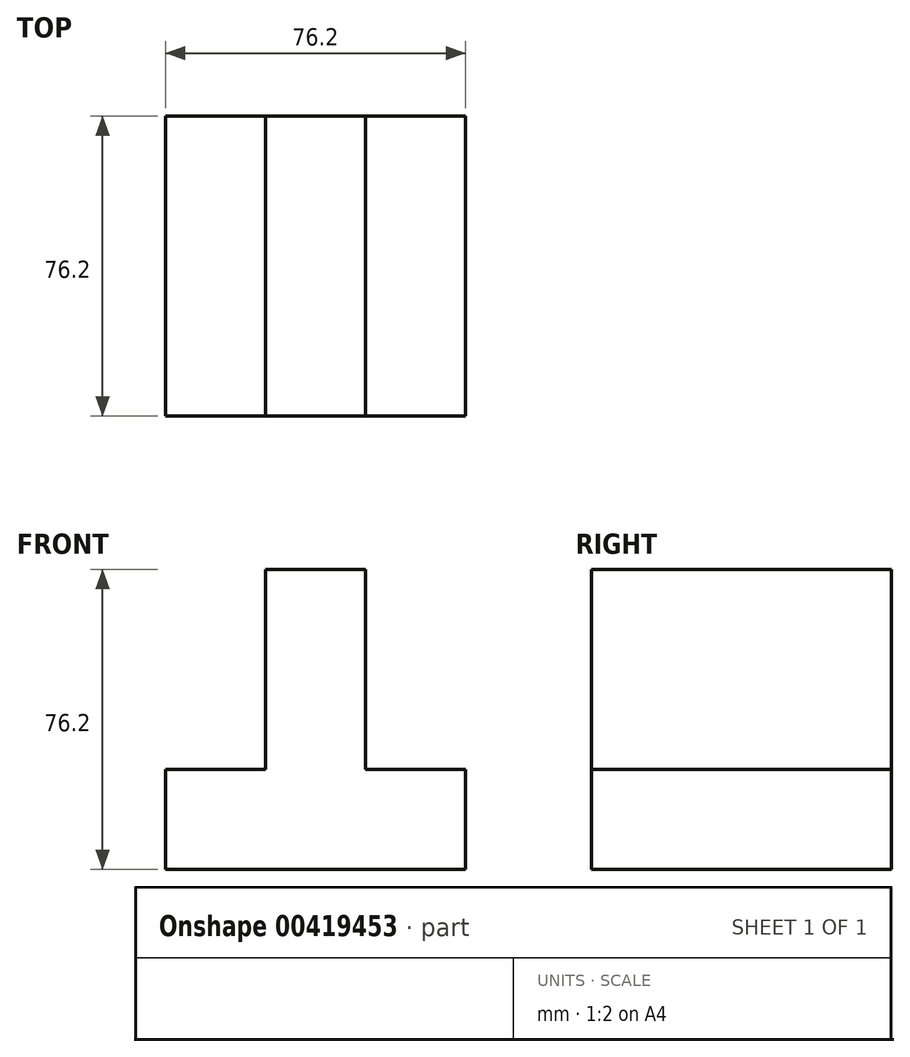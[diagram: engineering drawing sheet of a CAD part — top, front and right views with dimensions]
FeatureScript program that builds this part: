
annotation { "Feature Type Name" : "Feature", "Feature Type Description" : "" }
export const myFeature = defineFeature(function(context is Context, id is Id, definition is map)
    precondition{}
    {
        {
            var Q0;
            Q0=qCreatedBy(makeId("Front.planeOp"),FACE);
            var sketch = newSketch(context, id + "F0", { "sketchPlane" : qUnion([Q0])});
            skLineSegment(sketch, "E0", {"start": v(-36.92, -45.54) * mm, "end": v(39.28, -45.54) * mm});
            skLineSegment(sketch, "E1", {"start": v(39.28, -45.54) * mm, "end": v(39.28, -20.14) * mm});
            skLineSegment(sketch, "E2", {"start": v(39.28, -20.14) * mm, "end": v(13.88, -20.14) * mm});
            skLineSegment(sketch, "E3", {"start": v(13.88, -20.14) * mm, "end": v(13.88, 30.66) * mm});
            skLineSegment(sketch, "E4", {"start": v(13.88, 30.66) * mm, "end": v(-11.52, 30.66) * mm});
            skLineSegment(sketch, "E5", {"start": v(-11.52, 30.66) * mm, "end": v(-11.52, -20.14) * mm});
            skLineSegment(sketch, "E6", {"start": v(-11.52, -20.14) * mm, "end": v(-36.92, -20.14) * mm});
            skLineSegment(sketch, "E7", {"start": v(-36.92, -20.14) * mm, "end": v(-36.92, -45.54) * mm});
            skSolve(sketch);
        }
        {
            var Q0;
            Q0=makeQuery(id+"F0.imprint","IMPRINT",FACE,{"disambiguationData":[TD([[makeQuery(id+"F0.imprint","IMPRINT",EDGE,{"derivedFrom":sQuery(id+"F0.wireOp",EDGE,"E0")}),1.0]])]});
            extrude(context, id + "F1", {"entities" : qUnion([Q0]), "depth" : 76.2 * mm});
        }
    });
